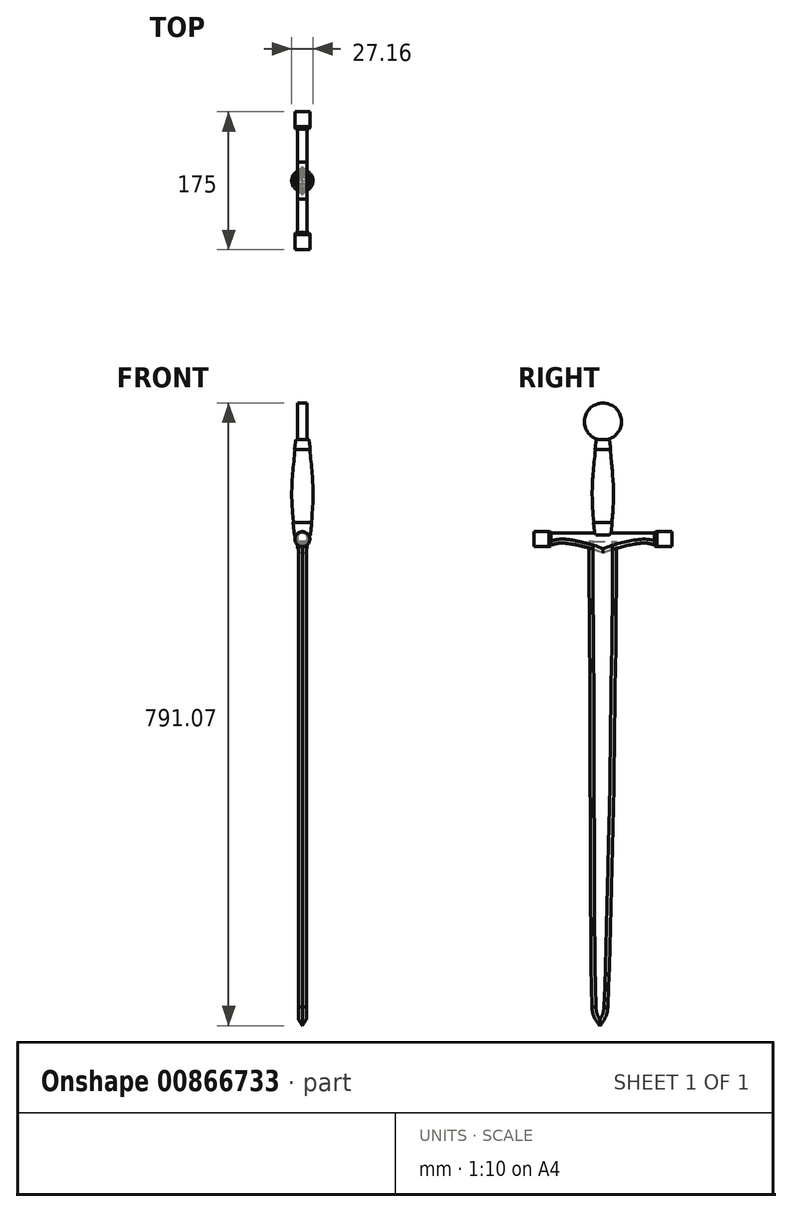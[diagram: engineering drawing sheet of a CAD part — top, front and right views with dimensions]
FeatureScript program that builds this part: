
annotation { "Feature Type Name" : "Feature", "Feature Type Description" : "" }
export const myFeature = defineFeature(function(context is Context, id is Id, definition is map)
    precondition{}
    {
        {
            var Q0;
            Q0=qCreatedBy(makeId("Right.planeOp"),FACE);
            var sketch = newSketch(context, id + "F0", { "sketchPlane" : qUnion([Q0])});
            skFitSpline(sketch, "E0", {"points": [v(15.7, 316.85) * mm, v(15.44, 255.83) * mm, v(14.96, 183.2) * mm, v(13.55, 114.23) * mm, v(12.35, 11.96) * mm, v(11.01, -48.46) * mm, v(9.54, -115.03) * mm, v(7.8, -186.55) * mm, v(6.57, -230.05) * mm, v(4.54, -274.5) * mm], "startDerivative": vector(8.51, -507.05) * mm, "endDerivative": vector(-24.21, -488.92) * mm});
            skFitSpline(sketch, "E1", {"points": [v(4.54, -274.5) * mm, v(-5.59, -298.39) * mm], "startDerivative": vector(0.63, -32.82) * mm, "endDerivative": vector(-13.34, -16.01) * mm});
            skFitSpline(sketch, "E2.MirrorCS", {"points": [v(-18.98, 316.87) * mm, v(-19.04, 251.48) * mm, v(-18.4, 181.8) * mm, v(-18.09, 112.43) * mm, v(-17.8, 12.24) * mm, v(-17.58, -48.2) * mm, v(-17.34, -114.78) * mm, v(-16.92, -186.32) * mm, v(-16.49, -229.84) * mm, v(-15.28, -274.31) * mm], "startDerivative": vector(-17.86, -506.8) * mm, "endDerivative": vector(15.2, -489.28) * mm});
            skFitSpline(sketch, "E3.MirrorCS", {"points": [v(-15.28, -274.31) * mm, v(-5.59, -298.39) * mm], "startDerivative": vector(-1.24, -32.8) * mm, "endDerivative": vector(13.04, -16.26) * mm});
            skLineSegment(sketch, "E4", {"start": v(-18.98, 316.87) * mm, "end": v(15.7, 316.85) * mm});
            skSolve(sketch);
        }
        {
            var Q0;
            Q0 = qSketchRegion(id + "F0", true);
            extrude(context, id + "F1", {"entities" : qUnion([Q0]), "depth" : 10 * mm, "offsetDistance" : 25 * mm, "symmetric" : true});
        }
        {
            var Q0;
            Q0=qCreatedBy(makeId("Right.planeOp"),FACE);
            var sketch = newSketch(context, id + "F2", { "sketchPlane" : qUnion([Q0])});
            skLineSegment(sketch, "E5", {"start": v(-1.64, 330.11) * mm, "end": v(-1.64, 427.76) * mm, "construction": true});
            skLineSegment(sketch, "E6.bottom", {"start": v(85.86, 329.29) * mm, "end": v(67.01, 329.29) * mm});
            skLineSegment(sketch, "E6.top", {"start": v(85.86, 319.79) * mm, "end": v(67.01, 319.79) * mm});
            skLineSegment(sketch, "E6.left", {"start": v(85.86, 329.29) * mm, "end": v(85.86, 319.79) * mm});
            skLineSegment(sketch, "E7", {"start": v(64.02, 328.44) * mm, "end": v(64.02, 319.79) * mm});
            skLineSegment(sketch, "E8", {"start": v(67.01, 319.79) * mm, "end": v(64.02, 319.79) * mm});
            skLineSegment(sketch, "E9", {"start": v(64.02, 328.44) * mm, "end": v(67.01, 329.29) * mm});
            skLineSegment(sketch, "E10.MirrorCS", {"start": v(-67.3, 328.44) * mm, "end": v(-70.3, 329.29) * mm});
            skLineSegment(sketch, "E11.MirrorCS", {"start": v(-70.3, 319.79) * mm, "end": v(-67.3, 319.79) * mm});
            skLineSegment(sketch, "E12.MirrorCS", {"start": v(-89.14, 329.29) * mm, "end": v(-89.14, 319.79) * mm});
            skLineSegment(sketch, "E13.MirrorCS", {"start": v(-89.14, 329.29) * mm, "end": v(-70.3, 329.29) * mm});
            skLineSegment(sketch, "E14.MirrorCS", {"start": v(-67.3, 328.44) * mm, "end": v(-67.3, 319.79) * mm});
            skLineSegment(sketch, "E15.MirrorCS", {"start": v(-89.14, 319.79) * mm, "end": v(-70.3, 319.79) * mm});
            skSolve(sketch);
        }
        {
            var Q0;
            Q0=makeQuery(id+"F2.imprint","IMPRINT",FACE,{"disambiguationData":[TD([[makeQuery(id+"F2.imprint","IMPRINT",EDGE,{"derivedFrom":sQuery(id+"F2.wireOp",EDGE,"E10.MirrorCS")}),1.0]])]});
            var Q1;
            Q1=makeQuery(id+"F2.imprint","IMPRINT",FACE,{"disambiguationData":[TD([[makeQuery(id+"F2.imprint","IMPRINT",EDGE,{"derivedFrom":sQuery(id+"F2.wireOp",EDGE,"E6.bottom")}),1.0]])]});
            var Q2;
            Q2=sQuery(id+"F2.wireOp",EDGE,"E15.MirrorCS");
            revolve(context, id + "F3", {"surfaceOperationType" : NewSurfaceOperationType.NEW, "entities" : qUnion([Q0, Q1]), "axis" : qUnion([Q2]), "revolveType" : RevolveType.FULL});
        }
        {
            var Q0;
            Q0=makeQuery(id+"F1.opExtrude","CAP_EDGE",EDGE,{"disambiguationData":[OSD([sQuery(id+"F0.wireOp",EDGE,"E0")])],"isStart":false});
            var Q1;
            Q1=makeQuery(id+"F1.opExtrude","CAP_EDGE",EDGE,{"disambiguationData":[OSD([sQuery(id+"F0.wireOp",EDGE,"E1")])],"isStart":false});
            var Q2;
            Q2=makeQuery(id+"F1.opExtrude","CAP_EDGE",EDGE,{"disambiguationData":[OSD([sQuery(id+"F0.wireOp",EDGE,"E2.MirrorCS")])],"isStart":false});
            var Q3;
            Q3=makeQuery(id+"F1.opExtrude","CAP_EDGE",EDGE,{"disambiguationData":[OSD([sQuery(id+"F0.wireOp",EDGE,"E3.MirrorCS")])],"isStart":false});
            var Q4;
            Q4=makeQuery(id+"F1.opExtrude","CAP_EDGE",EDGE,{"disambiguationData":[OSD([sQuery(id+"F0.wireOp",EDGE,"E0")])],"isStart":true});
            var Q5;
            Q5=makeQuery(id+"F1.opExtrude","CAP_EDGE",EDGE,{"disambiguationData":[OSD([sQuery(id+"F0.wireOp",EDGE,"E1")])],"isStart":true});
            var Q6;
            Q6=makeQuery(id+"F1.opExtrude","CAP_EDGE",EDGE,{"disambiguationData":[OSD([sQuery(id+"F0.wireOp",EDGE,"E3.MirrorCS")])],"isStart":true});
            var Q7;
            Q7=makeQuery(id+"F1.opExtrude","CAP_EDGE",EDGE,{"disambiguationData":[OSD([sQuery(id+"F0.wireOp",EDGE,"E2.MirrorCS")])],"isStart":true});
            chamfer(context, id + "F4", {"entities" : qUnion([Q0, Q1, Q2, Q3, Q4, Q5, Q6, Q7]), "width" : 5 * mm, "tangentPropagation" : true});
        }
        {
            var Q0;
            Q0=qCreatedBy(makeId("Right.planeOp"),FACE);
            var sketch = newSketch(context, id + "F5", { "sketchPlane" : qUnion([Q0])});
            skLineSegment(sketch, "E16", {"start": v(-68.17, 327.62) * mm, "end": v(65.33, 327.62) * mm});
            skLineSegment(sketch, "E17", {"start": v(65.33, 327.62) * mm, "end": v(65.33, 312.62) * mm});
            skLineSegment(sketch, "E18", {"start": v(65.33, 312.62) * mm, "end": v(63.6, 312.62) * mm});
            skLineSegment(sketch, "E19", {"start": v(-68.17, 327.62) * mm, "end": v(-68.17, 312.62) * mm});
            skLineSegment(sketch, "E20", {"start": v(-68.17, 312.62) * mm, "end": v(-66.43, 312.62) * mm});
            skLineSegment(sketch, "E21", {"start": v(-1.42, 321.46) * mm, "end": v(-1.42, 302.29) * mm});
            skFitSpline(sketch, "E22", {"points": [v(-66.43, 312.62) * mm, v(-56.21, 314.74) * mm, v(-36.29, 312.62) * mm, v(-1.42, 302.29) * mm], "startDerivative": vector(40.4, 11.55) * mm, "endDerivative": vector(74.12, -32.6) * mm});
            skFitSpline(sketch, "E23.MirrorCS", {"points": [v(63.6, 312.62) * mm, v(53.37, 314.74) * mm, v(33.45, 312.62) * mm, v(-1.42, 302.29) * mm], "startDerivative": vector(-40.4, 11.55) * mm, "endDerivative": vector(-74.12, -32.6) * mm});
            skSolve(sketch);
        }
        {
            var Q0;
            Q0=makeQuery(id+"F5.imprint","IMPRINT",FACE,{"disambiguationData":[TD([[makeQuery(id+"F5.imprint","IMPRINT",EDGE,{"derivedFrom":sQuery(id+"F5.wireOp",EDGE,"E16")}),-1.0]])]});
            extrude(context, id + "F6", {"entities" : qUnion([Q0]), "depth" : 12 * mm, "offsetDistance" : 25 * mm, "symmetric" : true});
        }
        {
            var Q0;
            Q0=makeQuery(id+"F6.opExtrude","CAP_EDGE",EDGE,{"disambiguationData":[OSD([sQuery(id+"F5.wireOp",EDGE,"E16")])],"isStart":false});
            var Q1;
            Q1=makeQuery(id+"F6.opExtrude","CAP_EDGE",EDGE,{"disambiguationData":[OSD([sQuery(id+"F5.wireOp",EDGE,"E16")])],"isStart":true});
            var Q2;
            Q2=makeQuery(id+"F6.opExtrude","CAP_EDGE",EDGE,{"disambiguationData":[OSD([sQuery(id+"F5.wireOp",EDGE,"E23.MirrorCS")])],"isStart":true});
            var Q3;
            Q3=makeQuery(id+"F6.opExtrude","CAP_EDGE",EDGE,{"disambiguationData":[OSD([sQuery(id+"F5.wireOp",EDGE,"E22")])],"isStart":true});
            var Q4;
            Q4=makeQuery(id+"F6.opExtrude","CAP_EDGE",EDGE,{"disambiguationData":[OSD([sQuery(id+"F5.wireOp",EDGE,"E23.MirrorCS")])],"isStart":false});
            var Q5;
            Q5=makeQuery(id+"F6.opExtrude","CAP_EDGE",EDGE,{"disambiguationData":[OSD([sQuery(id+"F5.wireOp",EDGE,"E22")])],"isStart":false});
            fillet(context, id + "F7", {"entities" : qUnion([Q0, Q1, Q2, Q3, Q4, Q5]), "radius" : 5 * mm, "tangentPropagation" : true, "allowEdgeOverflow" : false});
        }
        {
            var Q0;
            Q0=qCreatedBy(makeId("Right.planeOp"),FACE);
            var sketch = newSketch(context, id + "F8", { "sketchPlane" : qUnion([Q0])});
            skLineSegment(sketch, "E24", {"start": v(6.6, 446.2) * mm, "end": v(-1.64, 446.2) * mm});
            skFitSpline(sketch, "E25", {"points": [v(6.6, 446.2) * mm, v(9.84, 418.06) * mm, v(11.75, 395.73) * mm, v(12.25, 367.67) * mm, v(9.58, 334.63) * mm, v(8.44, 324.9) * mm], "startDerivative": vector(16.88, -86.61) * mm, "endDerivative": vector(-7.07, -56.28) * mm});
            skLineSegment(sketch, "E26", {"start": v(8.44, 324.9) * mm, "end": v(-1.64, 324.9) * mm});
            skLineSegment(sketch, "E27", {"start": v(-1.64, 446.2) * mm, "end": v(-1.64, 324.9) * mm});
            skFitSpline(sketch, "E28.0", {"points": [v(6.12, 446.1) * mm, v(6.46, 444.32) * mm, v(6.97, 440.91) * mm, v(7.62, 435.52) * mm, v(8.08, 431.2) * mm, v(8.52, 426.76) * mm, v(8.94, 422.33) * mm, v(9.34, 418.06) * mm, v(9.7, 414.11) * mm, v(10.05, 410.41) * mm, v(10.37, 406.89) * mm, v(10.67, 403.47) * mm, v(10.94, 400.09) * mm, v(11.2, 396.67) * mm, v(11.42, 393.14) * mm, v(11.62, 389.48) * mm, v(11.78, 385.68) * mm, v(11.88, 381.73) * mm, v(11.93, 377.63) * mm, v(11.9, 373.37) * mm, v(11.8, 368.94) * mm, v(11.6, 364.32) * mm, v(11.33, 359.6) * mm, v(11, 354.85) * mm, v(10.49, 348.62) * mm, v(9.93, 342.74) * mm, v(9.4, 337.59) * mm, v(9.03, 334.18) * mm, v(8.7, 331.3) * mm, v(8.33, 328.05) * mm, v(8.1, 326.13) * mm, v(7.95, 324.96) * mm]});
            skLineSegment(sketch, "E29", {"start": v(9.72, 340.76) * mm, "end": v(10.22, 340.76) * mm});
            skLineSegment(sketch, "E30", {"start": v(7.8, 433.87) * mm, "end": v(8.3, 433.87) * mm});
            skLineSegment(sketch, "E31", {"start": v(9.72, 340.76) * mm, "end": v(-1.64, 340.76) * mm});
            skLineSegment(sketch, "E32", {"start": v(7.8, 433.87) * mm, "end": v(-1.64, 433.87) * mm});
            skSolve(sketch);
        }
        {
            var Q0;
            Q0=makeQuery(id+"F8.imprint","IMPRINT",FACE,{"disambiguationData":[TD([[makeQuery(id+"F8.imprint","IMPRINT",EDGE,{"derivedFrom":sQuery(id+"F8.wireOp",EDGE,"E24")}),1.0]])]});
            var Q1;
            {var subQ1=sQuery(id+"F8.wireOp",EDGE,"E26");Q1=makeQuery(id+"F8.imprint","IMPRINT",FACE,{"disambiguationData":[TD([[makeQuery(id+"F8.imprint","IMPRINT",EDGE,{"derivedFrom":subQ1}),-1.0]])]});}
            var Q2;
            Q2=sQuery(id+"F8.wireOp",EDGE,"E27");
            revolve(context, id + "F9", {"operationType" : NewBodyOperationType.ADD, "surfaceOperationType" : NewSurfaceOperationType.NEW, "entities" : qUnion([Q0, Q1]), "axis" : qUnion([Q2]), "revolveType" : RevolveType.FULL});
        }
        {
            var Q0;
            Q0=qCreatedBy(makeId("Right.planeOp"),FACE);
            var sketch = newSketch(context, id + "F10", { "sketchPlane" : qUnion([Q0])});
            skCircle(sketch, "E33", {"center": v(-1.56, 469.1) * mm, "radius": 23.58 * mm});
            skSolve(sketch);
        }
        {
            var Q0;
            Q0=makeQuery(id+"F10.imprint","IMPRINT",FACE,{"disambiguationData":[TD([[makeQuery(id+"F10.imprint","IMPRINT",EDGE,{"derivedFrom":sQuery(id+"F10.wireOp",EDGE,"E33")}),1.0]])]});
            extrude(context, id + "F11", {"entities" : qUnion([Q0]), "operationType" : NewBodyOperationType.ADD, "depth" : 12 * mm, "offsetDistance" : 25 * mm, "symmetric" : true});
        }
        {
            var Q0;
            Q0=makeQuery(id+"F8.imprint","IMPRINT",FACE,{"disambiguationData":[TD([[makeQuery(id+"F8.imprint","IMPRINT",EDGE,{"derivedFrom":sQuery(id+"F8.wireOp",EDGE,"E28.0")}),-1.0]])]});
            var Q1;
            Q1=sQuery(id+"F8.wireOp",EDGE,"E27");
            revolve(context, id + "F12", {"surfaceOperationType" : NewSurfaceOperationType.NEW, "entities" : qUnion([Q0]), "axis" : qUnion([Q1]), "revolveType" : RevolveType.FULL});
        }
    });
